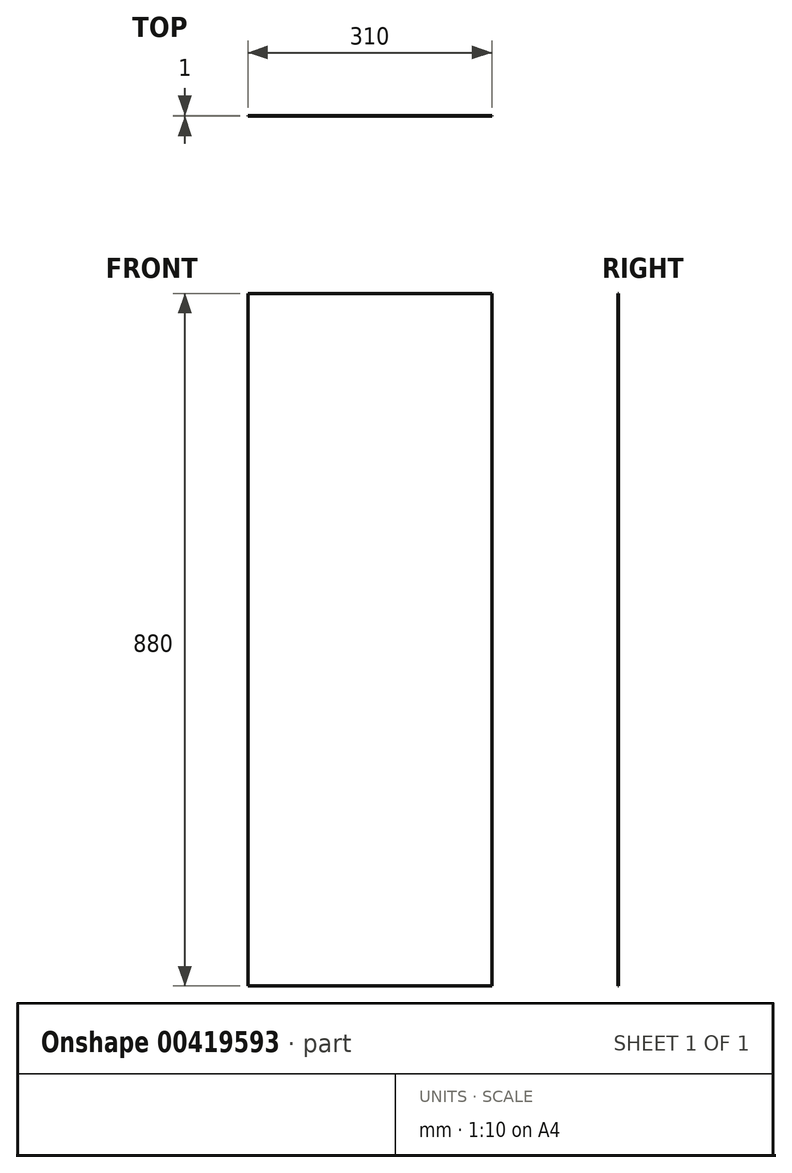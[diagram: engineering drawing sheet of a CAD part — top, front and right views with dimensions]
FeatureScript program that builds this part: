
annotation { "Feature Type Name" : "Feature", "Feature Type Description" : "" }
export const myFeature = defineFeature(function(context is Context, id is Id, definition is map)
    precondition{}
    {
        {
            var Q0;
            Q0=qCreatedBy(makeId("Front.planeOp"),FACE);
            var sketch = newSketch(context, id + "F0", { "sketchPlane" : qUnion([Q0])});
            skLineSegment(sketch, "E0.bottom", {"start": v(255.55, 844) * mm, "end": v(-54.45, 844) * mm});
            skLineSegment(sketch, "E0.top", {"start": v(255.55, -36) * mm, "end": v(-54.45, -36) * mm});
            skLineSegment(sketch, "E0.left", {"start": v(255.55, 844) * mm, "end": v(255.55, -36) * mm});
            skLineSegment(sketch, "E0.right", {"start": v(-54.45, 844) * mm, "end": v(-54.45, -36) * mm});
            skSolve(sketch);
        }
        {
            var Q0;
            Q0=makeQuery(id+"F0.imprint","IMPRINT",FACE,{"disambiguationData":[TD([[makeQuery(id+"F0.imprint","IMPRINT",EDGE,{"derivedFrom":sQuery(id+"F0.wireOp",EDGE,"E0.bottom")}),1.0]])]});
            extrude(context, id + "F1", {"entities" : qUnion([Q0]), "depth" : 1 * mm});
        }
    });
